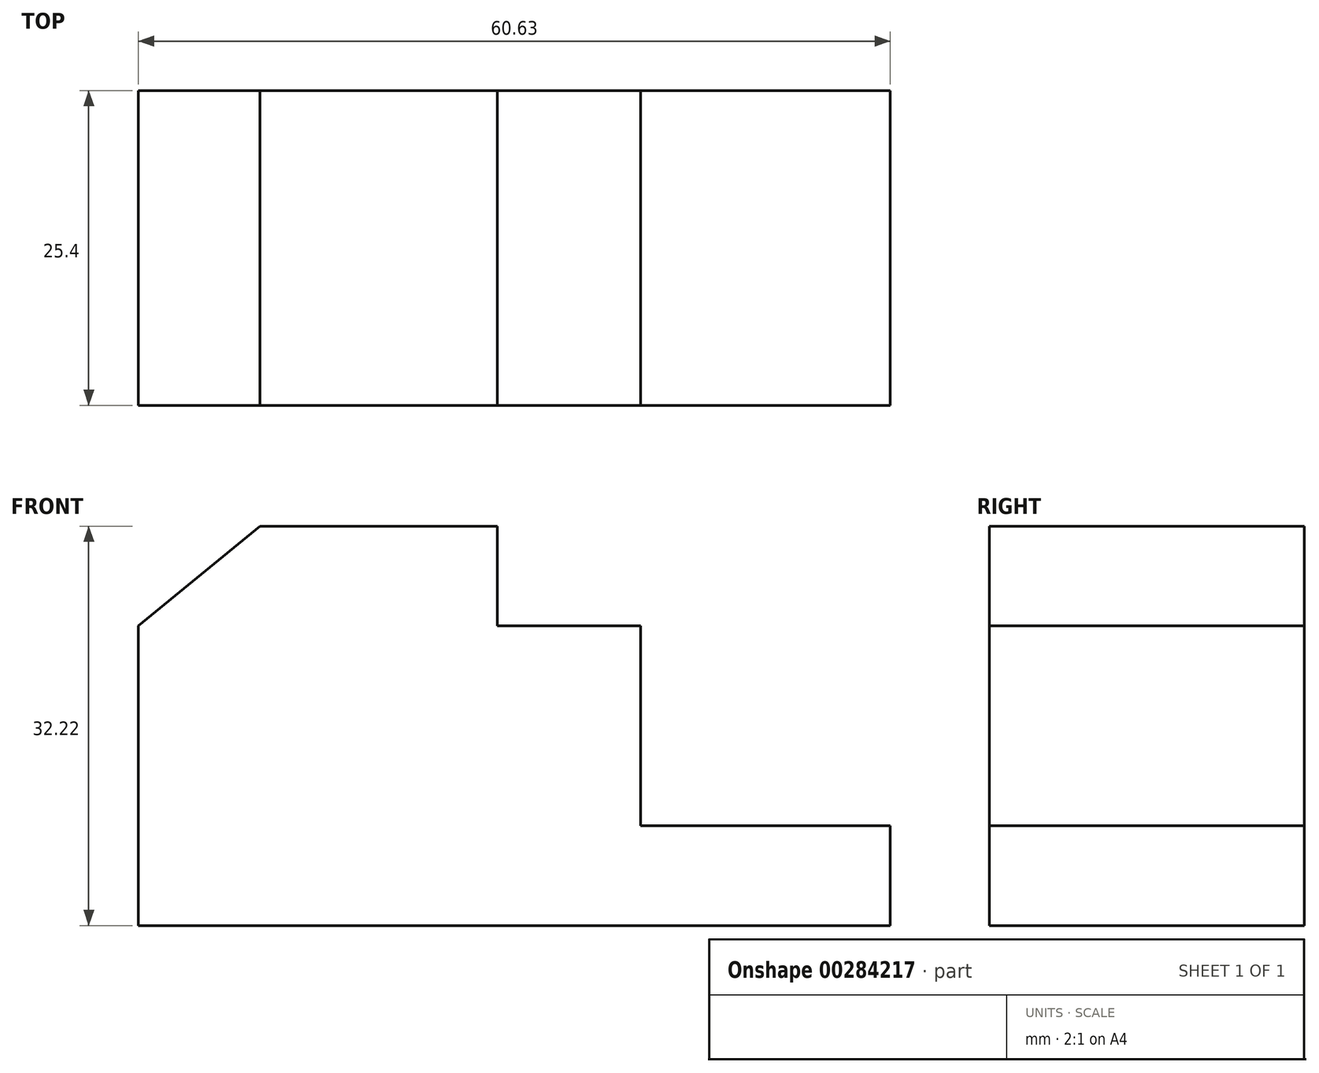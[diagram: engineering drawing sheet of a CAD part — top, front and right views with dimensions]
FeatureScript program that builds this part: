
annotation { "Feature Type Name" : "Feature", "Feature Type Description" : "" }
export const myFeature = defineFeature(function(context is Context, id is Id, definition is map)
    precondition{}
    {
        {
            var Q0;
            Q0=qCreatedBy(makeId("Front.planeOp"),FACE);
            var sketch = newSketch(context, id + "F0", { "sketchPlane" : qUnion([Q0])});
            skLineSegment(sketch, "E0", {"start": v(0, 0) * mm, "end": v(0, 8.06) * mm});
            skLineSegment(sketch, "E1", {"start": v(0, 8.06) * mm, "end": v(-20.14, 8.06) * mm});
            skLineSegment(sketch, "E2", {"start": v(-20.14, 8.06) * mm, "end": v(-20.14, 24.17) * mm});
            skLineSegment(sketch, "E3", {"start": v(-20.14, 24.17) * mm, "end": v(-31.68, 24.17) * mm});
            skLineSegment(sketch, "E4", {"start": v(-31.68, 24.17) * mm, "end": v(-31.68, 32.22) * mm});
            skLineSegment(sketch, "E5", {"start": v(-31.68, 32.22) * mm, "end": v(-50.84, 32.22) * mm});
            skLineSegment(sketch, "E6", {"start": v(-50.84, 32.22) * mm, "end": v(-60.63, 24.17) * mm});
            skLineSegment(sketch, "E7", {"start": v(-60.63, 24.17) * mm, "end": v(-60.63, 0) * mm});
            skLineSegment(sketch, "E8", {"start": v(-60.63, 0) * mm, "end": v(0, 0) * mm});
            skLineSegment(sketch, "E9", {"start": v(-50.84, 32.22) * mm, "end": v(-50.84, 16.11) * mm});
            skPoint(sketch, "E9.endSnap0", {"position": v(-20.14, 16.11) * mm});
            skLineSegment(sketch, "E10", {"start": v(-50.84, 16.11) * mm, "end": v(-20.14, 16.11) * mm});
            skSolve(sketch);
        }
        {
            var Q0;
            {var subQ0=sQuery(id+"F0.wireOp",EDGE,"E3");Q0=makeQuery(id+"F0.imprint","IMPRINT",FACE,{"disambiguationData":[TD([[makeQuery(id+"F0.imprint","IMPRINT",EDGE,{"derivedFrom":subQ0}),1.0]])]});}
            var Q1;
            Q1=makeQuery(id+"F0.imprint","IMPRINT",FACE,{"disambiguationData":[TD([[makeQuery(id+"F0.imprint","IMPRINT",EDGE,{"derivedFrom":sQuery(id+"F0.wireOp",EDGE,"E0")}),1.0]])]});
            extrude(context, id + "F1", {"entities" : qUnion([Q0, Q1]), "endBound" : BoundingType.SYMMETRIC, "depth" : 25.4 * mm});
        }
    });
